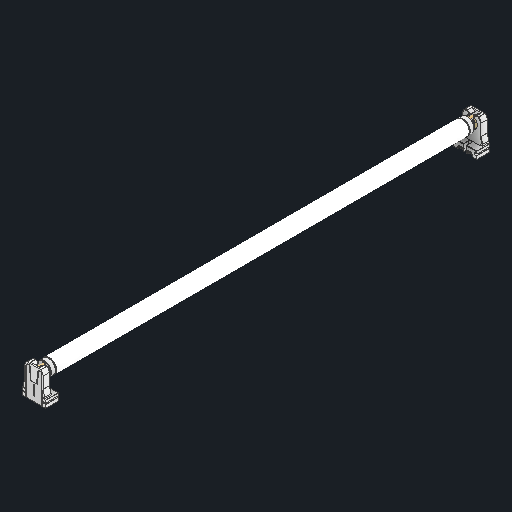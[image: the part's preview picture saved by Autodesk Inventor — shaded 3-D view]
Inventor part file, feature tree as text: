
AUTODESK INVENTOR PART (.ipt)
format: ipt  version: 2024 (Build 280153000, 153)  size: 1,354,240 bytes
history: native  units: mm
features: other x23, extrude x2, sketch x1
ambient origin geometry x8: Origin, YZ Plane, XZ Plane, XY Plane, X Axis, Y Axis, Z Axis, Center Point
bodies: Solid1 (feature_tree), Solid2 (feature_tree), Solid3 (feature_tree), Solid4 (feature_tree), Solid5 (feature_tree), Solid6 (feature_tree), Solid7 (feature_tree), Solid8 (feature_tree), Solid9 (feature_tree), Solid10 (feature_tree), Solid11 (feature_tree), Solid12 (feature_tree), Solid13 (feature_tree), Solid14 (feature_tree), Solid15 (feature_tree), Solid16 (feature_tree), Solid17 (feature_tree), Solid18 (feature_tree), Solid19 (feature_tree), Solid20 (feature_tree), Solid21 (feature_tree)
feature tree (26):
  other  "Lámpara Fluorescente T8.ipt"
  sketch  "Boceto1"  dims[d0=10000.0mm d1=1.0mm d2=5.0mm d3=1.0mm d4=0.0mm d5=1.0mm d6=5.0mm d7=1.0mm d8=0.0mm]
  extrude  "Extrusión1"  Depth=1.0mm
  extrude  "Extrusión2"  Depth=5.0mm
  other  "Solid1::Lámpara Fluorescente T8.ipt"
  other  "Solid2::Lámpara Fluorescente T8.ipt"
  other  "Solid3::Lámpara Fluorescente T8.ipt"
  other  "Solid4::Lámpara Fluorescente T8.ipt"
  other  "Solid5::Lámpara Fluorescente T8.ipt"
  other  "Solid6::Lámpara Fluorescente T8.ipt"
  other  "Solid7::Lámpara Fluorescente T8.ipt"
  other  "Solid8::Lámpara Fluorescente T8.ipt"
  other  "Solid9::Lámpara Fluorescente T8.ipt"
  other  "Solid10::Lámpara Fluorescente T8.ipt"
  other  "Solid11::Lámpara Fluorescente T8.ipt"
  other  "Solid12::Lámpara Fluorescente T8.ipt"
  other  "Solid13::Lámpara Fluorescente T8.ipt"
  other  "Solid14::Lámpara Fluorescente T8.ipt"
  other  "Solid15::Lámpara Fluorescente T8.ipt"
  other  "Solid16::Lámpara Fluorescente T8.ipt"
  other  "Solid17::Lámpara Fluorescente T8.ipt"
  other  "Solid18::Lámpara Fluorescente T8.ipt"
  other  "Solid19::Lámpara Fluorescente T8.ipt"
  other  "Solid20::Lámpara Fluorescente T8.ipt"
  other  "Solid21::Lámpara Fluorescente T8.ipt"
  other  "OperaciónIdentificador1"
